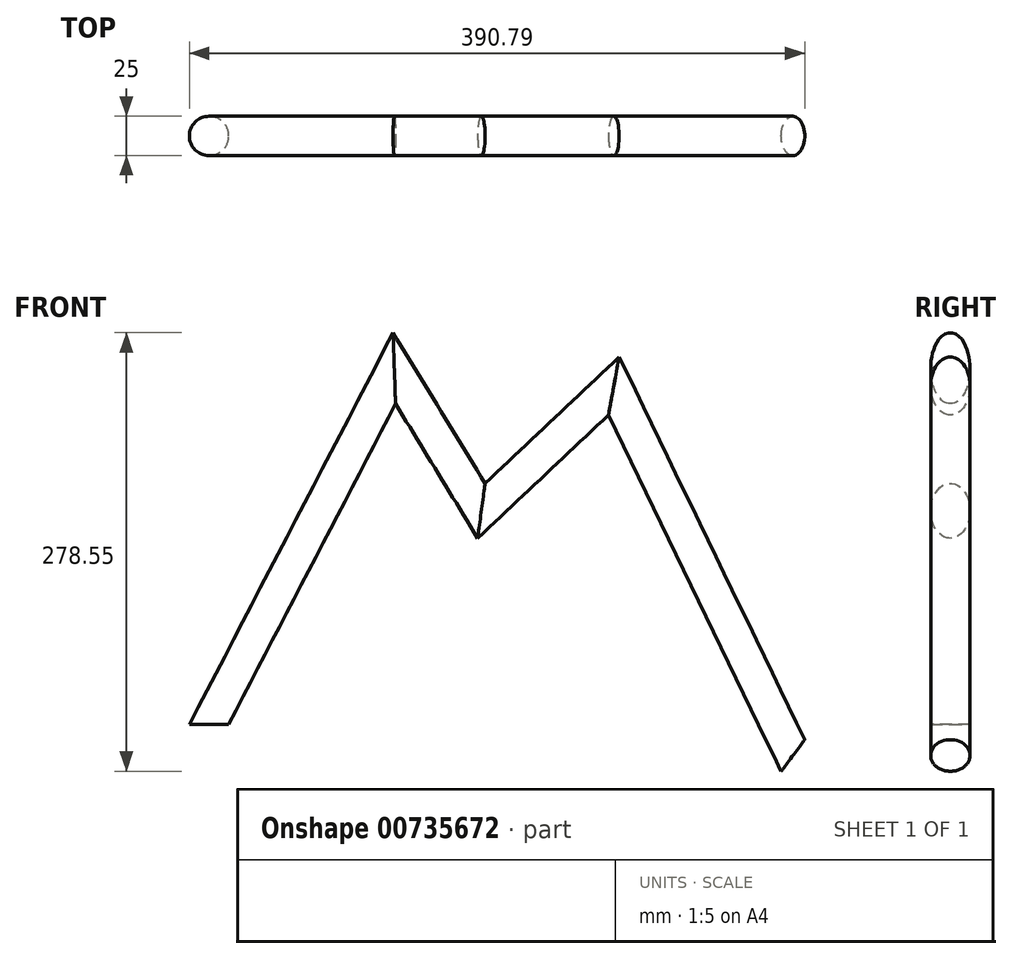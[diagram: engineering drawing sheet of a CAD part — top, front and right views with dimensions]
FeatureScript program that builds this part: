
annotation { "Feature Type Name" : "Feature", "Feature Type Description" : "" }
export const myFeature = defineFeature(function(context is Context, id is Id, definition is map)
    precondition{}
    {
        {
            var Q0;
            Q0=qCreatedBy(makeId("Top.planeOp"),FACE);
            var sketch = newSketch(context, id + "F0", { "sketchPlane" : qUnion([Q0])});
            skCircle(sketch, "E0", {"center": v(0, 0) * mm, "radius": 12.5 * mm});
            skSolve(sketch);
        }
        {
            var Q0;
            Q0=qCreatedBy(makeId("Front.planeOp"),FACE);
            var sketch = newSketch(context, id + "F1", { "sketchPlane" : qUnion([Q0])});
            skLineSegment(sketch, "E1", {"start": v(0, 0) * mm, "end": v(117.65, 226.18) * mm});
            skLineSegment(sketch, "E2", {"start": v(117.65, 226.18) * mm, "end": v(172.93, 135.64) * mm});
            skLineSegment(sketch, "E3", {"start": v(172.93, 135.64) * mm, "end": v(257.06, 214.96) * mm});
            skLineSegment(sketch, "E4", {"start": v(257.06, 214.96) * mm, "end": v(370.83, -19.8) * mm});
            skSolve(sketch);
        }
        {
            var Q0;
            Q0 = qSketchRegion(id + "F0", true);
            var Q1;
            Q1 = qConstructionFilter(qBodyType(qCreatedBy(id + "F1" ,EDGE), BodyType.WIRE), ConstructionObject.NO);
            sweep(context, id + "F2", {"profiles" : qUnion([Q0]), "path" : qUnion([Q1])});
        }
    });
